# Revit family: Furniture_Office-Dividers&Screens_Clestra_Phone-Booth_London
name_source: partatom
category: Modèles génériques
revit_build: Autodesk Revit 2018 (Build: 20180329_1100(x64)
units: mm (PartAtom-declared; Revit-internal decimal feet)

## family parameters
Basée sur le plan de construction = Non
Cote de connecteur circulaire = Utiliser le diamètre
Couper avec des vides une fois chargée = Non
Numéro OmniClass = 23.40.00.00
Partagée = Non
Peut héberger une armature = Non
Point de calcul de pièce = Non
Titre OmniClass = Equipment and Furnishings
Toujours verticalement = Oui
Type d'élément = Normal

## types (1)
- PhoneBooth LONDON
    Code d'assemblage = E
    Description = The London model of the Royal phone booth range offers an acoustically-insulated space in which you can conduct conversations in peace and quiet. Thanks to the efficient acoustic qualities of Clestra Hauserman prefabricated partitions and ceiling panels, the London booth ensures conversations remain private and confidential. Free-standing and independent of the building structure, the London phone booth can be installed in any office environment and is easily moved according to individual requirements.
    Edition number = 1
    Fabricant = CLESTRA HAUSERMAN
    Height = 2438 mm
    Modèle = LONDON
    Note d'identification = N
    Product Guid = c70c1fa6-de0a-4e38-8ef6-280050107113
    Product data url = https://bimobject.com
    URL = clestra.com
    Width = 1100 mm  [stored 3.60892 ft]

note: [stored X ft] marks values corroborated as IEEE doubles in the binary element streams (Revit-internal decimal feet)
